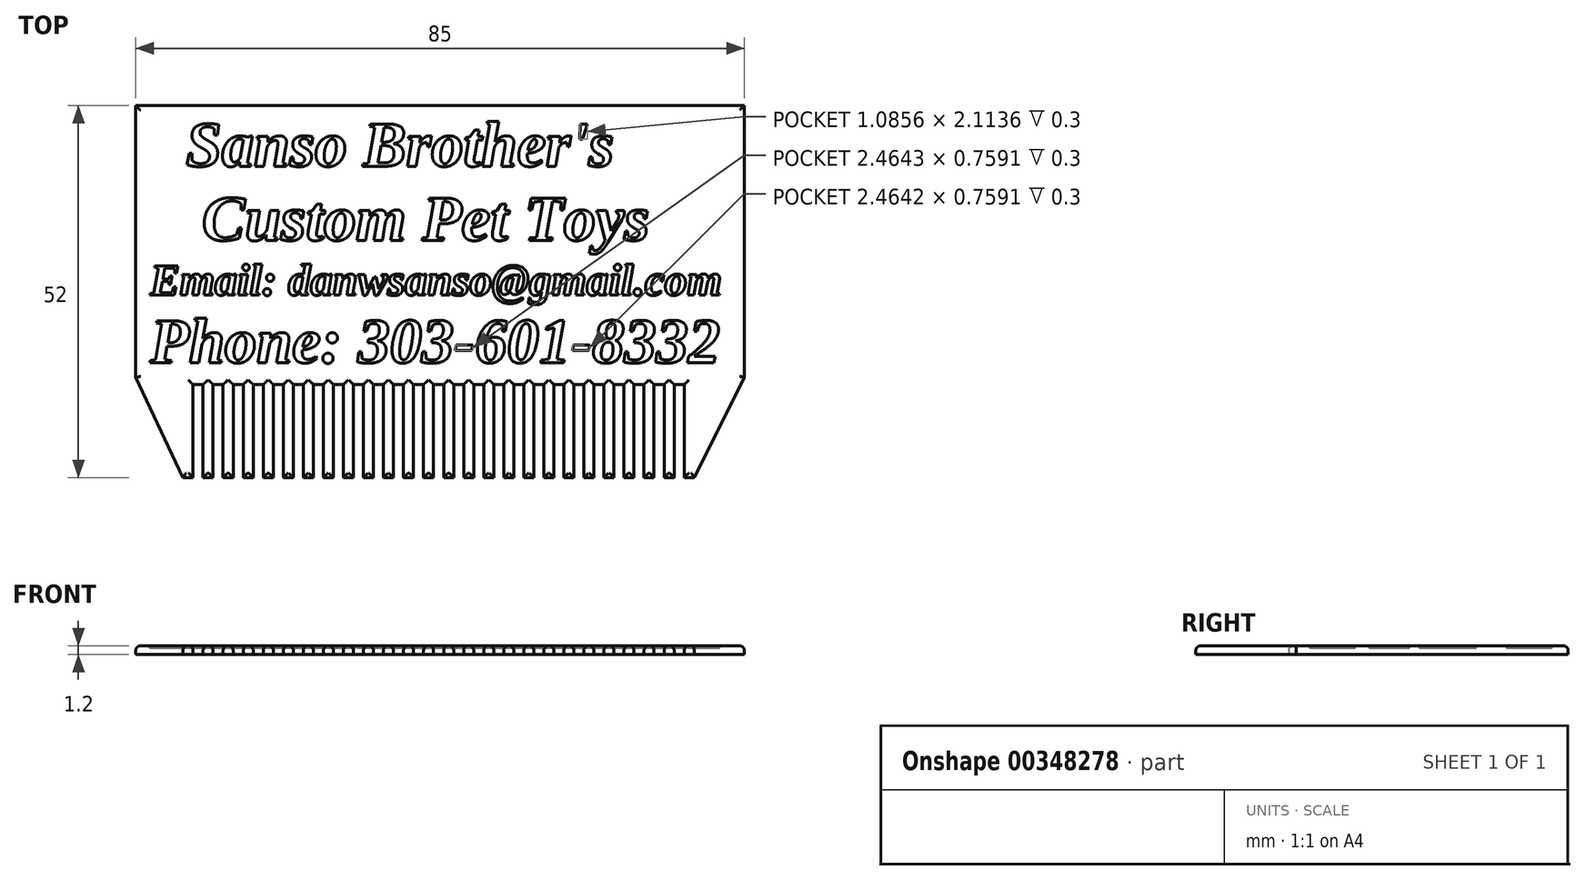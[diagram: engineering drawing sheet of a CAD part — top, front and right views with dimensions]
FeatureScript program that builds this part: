
annotation { "Feature Type Name" : "Feature", "Feature Type Description" : "" }
export const myFeature = defineFeature(function(context is Context, id is Id, definition is map)
    precondition{}
    {
        {
            var Q0;
            Q0=qCreatedBy(makeId("Top.planeOp"),FACE);
            var sketch = newSketch(context, id + "F0", { "sketchPlane" : qUnion([Q0])});
            skLineSegment(sketch, "E0.bottom", {"start": v(-26, -42.5) * mm, "end": v(-26, -80.5) * mm});
            skLineSegment(sketch, "E0.top", {"start": v(59, -42.5) * mm, "end": v(59, -80.5) * mm});
            skLineSegment(sketch, "E0.left", {"start": v(-26, -42.5) * mm, "end": v(59, -42.5) * mm});
            skLineSegment(sketch, "E0.right", {"start": v(-19.4, -94.5) * mm, "end": v(-18, -94.5) * mm});
            skPoint(sketch, "E0.middle", {"position": v(16.5, -68.5) * mm});
            skLineSegment(sketch, "E1", {"start": v(-18, -94.5) * mm, "end": v(-18, -81.5) * mm});
            skLineSegment(sketch, "E2", {"start": v(-18, -81.5) * mm, "end": v(-16.6, -81.5) * mm});
            skLineSegment(sketch, "E3", {"start": v(-16.6, -81.5) * mm, "end": v(-16.6, -94.5) * mm});
            skLineSegment(sketch, "E4.0.1.0", {"start": v(-16.6, -94.5) * mm, "end": v(-16.6, -81.5) * mm});
            skLineSegment(sketch, "E4.0.1.1", {"start": v(-15.2, -81.5) * mm, "end": v(-15.2, -94.5) * mm});
            skLineSegment(sketch, "E4.0.2.0", {"start": v(-15.2, -94.5) * mm, "end": v(-15.2, -81.5) * mm});
            skLineSegment(sketch, "E4.0.2.1", {"start": v(-13.8, -81.5) * mm, "end": v(-13.8, -94.5) * mm});
            skLineSegment(sketch, "E4.0.2.2", {"start": v(-15.2, -81.5) * mm, "end": v(-13.8, -81.5) * mm});
            skLineSegment(sketch, "E4.0.3.0", {"start": v(-13.8, -94.5) * mm, "end": v(-13.8, -81.5) * mm});
            skLineSegment(sketch, "E4.0.3.1", {"start": v(-12.4, -81.5) * mm, "end": v(-12.4, -94.5) * mm});
            skLineSegment(sketch, "E4.0.4.0", {"start": v(-12.4, -94.5) * mm, "end": v(-12.4, -81.5) * mm});
            skLineSegment(sketch, "E4.0.4.1", {"start": v(-11, -81.5) * mm, "end": v(-11, -94.5) * mm});
            skLineSegment(sketch, "E4.0.4.2", {"start": v(-12.4, -81.5) * mm, "end": v(-11, -81.5) * mm});
            skLineSegment(sketch, "E4.0.5.0", {"start": v(-11, -94.5) * mm, "end": v(-11, -81.5) * mm});
            skLineSegment(sketch, "E4.0.5.1", {"start": v(-9.6, -81.5) * mm, "end": v(-9.6, -94.5) * mm});
            skLineSegment(sketch, "E4.0.6.0", {"start": v(-9.6, -94.5) * mm, "end": v(-9.6, -81.5) * mm});
            skLineSegment(sketch, "E4.0.6.1", {"start": v(-8.2, -81.5) * mm, "end": v(-8.2, -94.5) * mm});
            skLineSegment(sketch, "E4.0.6.2", {"start": v(-9.6, -81.5) * mm, "end": v(-8.2, -81.5) * mm});
            skLineSegment(sketch, "E4.0.7.0", {"start": v(-8.2, -94.5) * mm, "end": v(-8.2, -81.5) * mm});
            skLineSegment(sketch, "E4.0.7.1", {"start": v(-6.8, -81.5) * mm, "end": v(-6.8, -94.5) * mm});
            skLineSegment(sketch, "E4.0.8.0", {"start": v(-6.8, -94.5) * mm, "end": v(-6.8, -81.5) * mm});
            skLineSegment(sketch, "E4.0.8.1", {"start": v(-5.4, -81.5) * mm, "end": v(-5.4, -94.5) * mm});
            skLineSegment(sketch, "E4.0.8.2", {"start": v(-6.8, -81.5) * mm, "end": v(-5.4, -81.5) * mm});
            skLineSegment(sketch, "E4.0.9.0", {"start": v(-5.4, -94.5) * mm, "end": v(-5.4, -81.5) * mm});
            skLineSegment(sketch, "E4.0.9.1", {"start": v(-4, -81.5) * mm, "end": v(-4, -94.5) * mm});
            skLineSegment(sketch, "E4.0.10.0", {"start": v(-4, -94.5) * mm, "end": v(-4, -81.5) * mm});
            skLineSegment(sketch, "E4.0.10.1", {"start": v(-2.6, -81.5) * mm, "end": v(-2.6, -94.5) * mm});
            skLineSegment(sketch, "E4.0.10.2", {"start": v(-4, -81.5) * mm, "end": v(-2.6, -81.5) * mm});
            skLineSegment(sketch, "E4.0.11.0", {"start": v(-2.6, -94.5) * mm, "end": v(-2.6, -81.5) * mm});
            skLineSegment(sketch, "E4.0.11.1", {"start": v(-1.2, -81.5) * mm, "end": v(-1.2, -94.5) * mm});
            skLineSegment(sketch, "E4.0.12.0", {"start": v(-1.2, -94.5) * mm, "end": v(-1.2, -81.5) * mm});
            skLineSegment(sketch, "E4.0.12.1", {"start": v(0.2, -81.5) * mm, "end": v(0.2, -94.5) * mm});
            skLineSegment(sketch, "E4.0.12.2", {"start": v(-1.2, -81.5) * mm, "end": v(0.2, -81.5) * mm});
            skLineSegment(sketch, "E4.0.13.0", {"start": v(0.2, -94.5) * mm, "end": v(0.2, -81.5) * mm});
            skLineSegment(sketch, "E4.0.13.1", {"start": v(1.6, -81.5) * mm, "end": v(1.6, -94.5) * mm});
            skLineSegment(sketch, "E4.0.14.0", {"start": v(1.6, -94.5) * mm, "end": v(1.6, -81.5) * mm});
            skLineSegment(sketch, "E4.0.14.1", {"start": v(3, -81.5) * mm, "end": v(3, -94.5) * mm});
            skLineSegment(sketch, "E4.0.14.2", {"start": v(1.6, -81.5) * mm, "end": v(3, -81.5) * mm});
            skLineSegment(sketch, "E4.0.15.0", {"start": v(3, -94.5) * mm, "end": v(3, -81.5) * mm});
            skLineSegment(sketch, "E4.0.15.1", {"start": v(4.4, -81.5) * mm, "end": v(4.4, -94.5) * mm});
            skLineSegment(sketch, "E4.0.16.0", {"start": v(4.4, -94.5) * mm, "end": v(4.4, -81.5) * mm});
            skLineSegment(sketch, "E4.0.16.1", {"start": v(5.8, -81.5) * mm, "end": v(5.8, -94.5) * mm});
            skLineSegment(sketch, "E4.0.16.2", {"start": v(4.4, -81.5) * mm, "end": v(5.8, -81.5) * mm});
            skLineSegment(sketch, "E4.0.17.0", {"start": v(5.8, -94.5) * mm, "end": v(5.8, -81.5) * mm});
            skLineSegment(sketch, "E4.0.17.1", {"start": v(7.2, -81.5) * mm, "end": v(7.2, -94.5) * mm});
            skLineSegment(sketch, "E4.0.18.0", {"start": v(7.2, -94.5) * mm, "end": v(7.2, -81.5) * mm});
            skLineSegment(sketch, "E4.0.18.1", {"start": v(8.6, -81.5) * mm, "end": v(8.6, -94.5) * mm});
            skLineSegment(sketch, "E4.0.18.2", {"start": v(7.2, -81.5) * mm, "end": v(8.6, -81.5) * mm});
            skLineSegment(sketch, "E4.0.19.0", {"start": v(8.6, -94.5) * mm, "end": v(8.6, -81.5) * mm});
            skLineSegment(sketch, "E4.0.19.1", {"start": v(10, -81.5) * mm, "end": v(10, -94.5) * mm});
            skLineSegment(sketch, "E4.0.20.0", {"start": v(10, -94.5) * mm, "end": v(10, -81.5) * mm});
            skLineSegment(sketch, "E4.0.20.1", {"start": v(11.4, -81.5) * mm, "end": v(11.4, -94.5) * mm});
            skLineSegment(sketch, "E4.0.20.2", {"start": v(10, -81.5) * mm, "end": v(11.4, -81.5) * mm});
            skLineSegment(sketch, "E4.0.21.0", {"start": v(11.4, -94.5) * mm, "end": v(11.4, -81.5) * mm});
            skLineSegment(sketch, "E4.0.21.1", {"start": v(12.8, -81.5) * mm, "end": v(12.8, -94.5) * mm});
            skLineSegment(sketch, "E4.0.22.0", {"start": v(12.8, -94.5) * mm, "end": v(12.8, -81.5) * mm});
            skLineSegment(sketch, "E4.0.22.1", {"start": v(14.2, -81.5) * mm, "end": v(14.2, -94.5) * mm});
            skLineSegment(sketch, "E4.0.22.2", {"start": v(12.8, -81.5) * mm, "end": v(14.2, -81.5) * mm});
            skLineSegment(sketch, "E4.0.23.0", {"start": v(14.2, -94.5) * mm, "end": v(14.2, -81.5) * mm});
            skLineSegment(sketch, "E4.0.23.1", {"start": v(15.6, -81.5) * mm, "end": v(15.6, -94.5) * mm});
            skLineSegment(sketch, "E4.0.24.0", {"start": v(15.6, -94.5) * mm, "end": v(15.6, -81.5) * mm});
            skLineSegment(sketch, "E4.0.24.1", {"start": v(17, -81.5) * mm, "end": v(17, -94.5) * mm});
            skLineSegment(sketch, "E4.0.24.2", {"start": v(15.6, -81.5) * mm, "end": v(17, -81.5) * mm});
            skLineSegment(sketch, "E4.0.25.0", {"start": v(17, -94.5) * mm, "end": v(17, -81.5) * mm});
            skLineSegment(sketch, "E4.0.25.1", {"start": v(18.4, -81.5) * mm, "end": v(18.4, -94.5) * mm});
            skLineSegment(sketch, "E4.0.26.0", {"start": v(18.4, -94.5) * mm, "end": v(18.4, -81.5) * mm});
            skLineSegment(sketch, "E4.0.26.1", {"start": v(19.8, -81.5) * mm, "end": v(19.8, -94.5) * mm});
            skLineSegment(sketch, "E4.0.26.2", {"start": v(18.4, -81.5) * mm, "end": v(19.8, -81.5) * mm});
            skLineSegment(sketch, "E4.0.27.0", {"start": v(19.8, -94.5) * mm, "end": v(19.8, -81.5) * mm});
            skLineSegment(sketch, "E4.0.27.1", {"start": v(21.2, -81.5) * mm, "end": v(21.2, -94.5) * mm});
            skLineSegment(sketch, "E4.0.28.0", {"start": v(21.2, -94.5) * mm, "end": v(21.2, -81.5) * mm});
            skLineSegment(sketch, "E4.0.28.1", {"start": v(22.6, -81.5) * mm, "end": v(22.6, -94.5) * mm});
            skLineSegment(sketch, "E4.0.28.2", {"start": v(21.2, -81.5) * mm, "end": v(22.6, -81.5) * mm});
            skLineSegment(sketch, "E4.0.29.0", {"start": v(22.6, -94.5) * mm, "end": v(22.6, -81.5) * mm});
            skLineSegment(sketch, "E4.0.29.1", {"start": v(24, -81.5) * mm, "end": v(24, -94.5) * mm});
            skLineSegment(sketch, "E4.0.30.0", {"start": v(24, -94.5) * mm, "end": v(24, -81.5) * mm});
            skLineSegment(sketch, "E4.0.30.1", {"start": v(25.4, -81.5) * mm, "end": v(25.4, -94.5) * mm});
            skLineSegment(sketch, "E4.0.30.2", {"start": v(24, -81.5) * mm, "end": v(25.4, -81.5) * mm});
            skLineSegment(sketch, "E4.0.31.0", {"start": v(25.4, -94.5) * mm, "end": v(25.4, -81.5) * mm});
            skLineSegment(sketch, "E4.0.31.1", {"start": v(26.8, -81.5) * mm, "end": v(26.8, -94.5) * mm});
            skLineSegment(sketch, "E4.0.32.0", {"start": v(26.8, -94.5) * mm, "end": v(26.8, -81.5) * mm});
            skLineSegment(sketch, "E4.0.32.1", {"start": v(28.2, -81.5) * mm, "end": v(28.2, -94.5) * mm});
            skLineSegment(sketch, "E4.0.32.2", {"start": v(26.8, -81.5) * mm, "end": v(28.2, -81.5) * mm});
            skLineSegment(sketch, "E4.0.33.0", {"start": v(28.2, -94.5) * mm, "end": v(28.2, -81.5) * mm});
            skLineSegment(sketch, "E4.0.33.1", {"start": v(29.6, -81.5) * mm, "end": v(29.6, -94.5) * mm});
            skLineSegment(sketch, "E4.0.34.0", {"start": v(29.6, -94.5) * mm, "end": v(29.6, -81.5) * mm});
            skLineSegment(sketch, "E4.0.34.1", {"start": v(31, -81.5) * mm, "end": v(31, -94.5) * mm});
            skLineSegment(sketch, "E4.0.34.2", {"start": v(29.6, -81.5) * mm, "end": v(31, -81.5) * mm});
            skLineSegment(sketch, "E4.0.35.0", {"start": v(31, -94.5) * mm, "end": v(31, -81.5) * mm});
            skLineSegment(sketch, "E4.0.35.1", {"start": v(32.4, -81.5) * mm, "end": v(32.4, -94.5) * mm});
            skLineSegment(sketch, "E4.0.36.0", {"start": v(32.4, -94.5) * mm, "end": v(32.4, -81.5) * mm});
            skLineSegment(sketch, "E4.0.36.1", {"start": v(33.8, -81.5) * mm, "end": v(33.8, -94.5) * mm});
            skLineSegment(sketch, "E4.0.36.2", {"start": v(32.4, -81.5) * mm, "end": v(33.8, -81.5) * mm});
            skLineSegment(sketch, "E4.0.37.0", {"start": v(33.8, -94.5) * mm, "end": v(33.8, -81.5) * mm});
            skLineSegment(sketch, "E4.0.37.1", {"start": v(35.2, -81.5) * mm, "end": v(35.2, -94.5) * mm});
            skLineSegment(sketch, "E4.0.38.0", {"start": v(35.2, -94.5) * mm, "end": v(35.2, -81.5) * mm});
            skLineSegment(sketch, "E4.0.38.1", {"start": v(36.6, -81.5) * mm, "end": v(36.6, -94.5) * mm});
            skLineSegment(sketch, "E4.0.38.2", {"start": v(35.2, -81.5) * mm, "end": v(36.6, -81.5) * mm});
            skLineSegment(sketch, "E4.0.39.0", {"start": v(36.6, -94.5) * mm, "end": v(36.6, -81.5) * mm});
            skLineSegment(sketch, "E4.0.39.1", {"start": v(38, -81.5) * mm, "end": v(38, -94.5) * mm});
            skLineSegment(sketch, "E4.0.40.0", {"start": v(38, -94.5) * mm, "end": v(38, -81.5) * mm});
            skLineSegment(sketch, "E4.0.40.1", {"start": v(39.4, -81.5) * mm, "end": v(39.4, -94.5) * mm});
            skLineSegment(sketch, "E4.0.40.2", {"start": v(38, -81.5) * mm, "end": v(39.4, -81.5) * mm});
            skLineSegment(sketch, "E4.0.41.0", {"start": v(39.4, -94.5) * mm, "end": v(39.4, -81.5) * mm});
            skLineSegment(sketch, "E4.0.41.1", {"start": v(40.8, -81.5) * mm, "end": v(40.8, -94.5) * mm});
            skLineSegment(sketch, "E4.0.42.0", {"start": v(40.8, -94.5) * mm, "end": v(40.8, -81.5) * mm});
            skLineSegment(sketch, "E4.0.42.1", {"start": v(42.2, -81.5) * mm, "end": v(42.2, -94.5) * mm});
            skLineSegment(sketch, "E4.0.42.2", {"start": v(40.8, -81.5) * mm, "end": v(42.2, -81.5) * mm});
            skLineSegment(sketch, "E4.0.43.0", {"start": v(42.2, -94.5) * mm, "end": v(42.2, -81.5) * mm});
            skLineSegment(sketch, "E4.0.43.1", {"start": v(43.6, -81.5) * mm, "end": v(43.6, -94.5) * mm});
            skLineSegment(sketch, "E4.0.44.0", {"start": v(43.6, -94.5) * mm, "end": v(43.6, -81.5) * mm});
            skLineSegment(sketch, "E4.0.44.1", {"start": v(45, -81.5) * mm, "end": v(45, -94.5) * mm});
            skLineSegment(sketch, "E4.0.44.2", {"start": v(43.6, -81.5) * mm, "end": v(45, -81.5) * mm});
            skLineSegment(sketch, "E4.0.45.0", {"start": v(45, -94.5) * mm, "end": v(45, -81.5) * mm});
            skLineSegment(sketch, "E4.0.45.1", {"start": v(46.4, -81.5) * mm, "end": v(46.4, -94.5) * mm});
            skLineSegment(sketch, "E4.0.46.0", {"start": v(46.4, -94.5) * mm, "end": v(46.4, -81.5) * mm});
            skLineSegment(sketch, "E4.0.46.1", {"start": v(47.8, -81.5) * mm, "end": v(47.8, -94.5) * mm});
            skLineSegment(sketch, "E4.0.46.2", {"start": v(46.4, -81.5) * mm, "end": v(47.8, -81.5) * mm});
            skLineSegment(sketch, "E4.0.47.0", {"start": v(47.8, -94.5) * mm, "end": v(47.8, -81.5) * mm});
            skLineSegment(sketch, "E4.0.47.1", {"start": v(49.2, -81.5) * mm, "end": v(49.2, -94.5) * mm});
            skLineSegment(sketch, "E4.0.48.0", {"start": v(49.2, -94.5) * mm, "end": v(49.2, -81.5) * mm});
            skLineSegment(sketch, "E4.0.48.1", {"start": v(50.6, -81.5) * mm, "end": v(50.6, -94.5) * mm});
            skLineSegment(sketch, "E4.0.48.2", {"start": v(49.2, -81.5) * mm, "end": v(50.6, -81.5) * mm});
            skLineSegment(sketch, "E4.0.49.0", {"start": v(50.6, -94.5) * mm, "end": v(50.6, -81.5) * mm});
            skLineSegment(sketch, "E4.direction1", {"start": v(-21.58, -80.5) * mm, "end": v(-21.58, -91.6) * mm, "construction": true});
            skLineSegment(sketch, "E4.direction2", {"start": v(-21.58, -80.5) * mm, "end": v(-17.6, -80.5) * mm, "construction": true});
            skLineSegment(sketch, "E5.trimOffspring", {"start": v(-16.6, -94.5) * mm, "end": v(-15.2, -94.5) * mm});
            skLineSegment(sketch, "E6.trimOffspring", {"start": v(-13.8, -94.5) * mm, "end": v(-12.4, -94.5) * mm});
            skLineSegment(sketch, "E7.trimOffspring", {"start": v(-11, -94.5) * mm, "end": v(-9.6, -94.5) * mm});
            skLineSegment(sketch, "E8.trimOffspring", {"start": v(-8.2, -94.5) * mm, "end": v(-6.8, -94.5) * mm});
            skLineSegment(sketch, "E9.trimOffspring", {"start": v(-5.4, -94.5) * mm, "end": v(-4, -94.5) * mm});
            skLineSegment(sketch, "E10.trimOffspring", {"start": v(-2.6, -94.5) * mm, "end": v(-1.2, -94.5) * mm});
            skLineSegment(sketch, "E11.trimOffspring", {"start": v(0.2, -94.5) * mm, "end": v(1.6, -94.5) * mm});
            skLineSegment(sketch, "E12.trimOffspring", {"start": v(3, -94.5) * mm, "end": v(4.4, -94.5) * mm});
            skLineSegment(sketch, "E13.trimOffspring", {"start": v(5.8, -94.5) * mm, "end": v(7.2, -94.5) * mm});
            skLineSegment(sketch, "E14.trimOffspring", {"start": v(8.6, -94.5) * mm, "end": v(10, -94.5) * mm});
            skLineSegment(sketch, "E15.trimOffspring", {"start": v(11.4, -94.5) * mm, "end": v(12.8, -94.5) * mm});
            skLineSegment(sketch, "E16.trimOffspring", {"start": v(14.2, -94.5) * mm, "end": v(15.6, -94.5) * mm});
            skLineSegment(sketch, "E17.trimOffspring", {"start": v(17, -94.5) * mm, "end": v(18.4, -94.5) * mm});
            skLineSegment(sketch, "E18.trimOffspring", {"start": v(19.8, -94.5) * mm, "end": v(21.2, -94.5) * mm});
            skLineSegment(sketch, "E19.trimOffspring", {"start": v(22.6, -94.5) * mm, "end": v(24, -94.5) * mm});
            skLineSegment(sketch, "E20.trimOffspring", {"start": v(25.4, -94.5) * mm, "end": v(26.8, -94.5) * mm});
            skLineSegment(sketch, "E21.trimOffspring", {"start": v(28.2, -94.5) * mm, "end": v(29.6, -94.5) * mm});
            skLineSegment(sketch, "E22.trimOffspring", {"start": v(31, -94.5) * mm, "end": v(32.4, -94.5) * mm});
            skLineSegment(sketch, "E23.trimOffspring", {"start": v(33.8, -94.5) * mm, "end": v(35.2, -94.5) * mm});
            skLineSegment(sketch, "E24.trimOffspring", {"start": v(36.6, -94.5) * mm, "end": v(38, -94.5) * mm});
            skLineSegment(sketch, "E25.trimOffspring", {"start": v(39.4, -94.5) * mm, "end": v(40.8, -94.5) * mm});
            skLineSegment(sketch, "E26.trimOffspring", {"start": v(42.2, -94.5) * mm, "end": v(43.6, -94.5) * mm});
            skLineSegment(sketch, "E27.trimOffspring", {"start": v(45, -94.5) * mm, "end": v(46.4, -94.5) * mm});
            skLineSegment(sketch, "E28.trimOffspring", {"start": v(47.8, -94.5) * mm, "end": v(49.2, -94.5) * mm});
            skLineSegment(sketch, "E29.trimOffspring", {"start": v(50.6, -94.5) * mm, "end": v(52, -94.5) * mm});
            skLineSegment(sketch, "E30", {"start": v(-19.4, -94.5) * mm, "end": v(-26, -80.5) * mm});
            skLineSegment(sketch, "E31", {"start": v(52, -94.5) * mm, "end": v(59, -80.5) * mm});
            skPoint(sketch, "E32.orphan", {"position": v(-26, -94.5) * mm});
            skPoint(sketch, "E33.orphan", {"position": v(59, -94.5) * mm});
            skSolve(sketch);
        }
        {
            var Q0;
            Q0 = qSketchRegion(id + "F0", true);
            extrude(context, id + "F1", {"entities" : qUnion([Q0]), "depth" : 1.2 * mm, "offsetDistance" : 25 * mm});
        }
        {
            var Q0;
            Q0=makeQuery(id+"F1.opExtrude","CAP_EDGE",EDGE,{"disambiguationData":[OSD([sQuery(id+"F0.wireOp",EDGE,"E5.trimOffspring")])],"isStart":false});
            var Q1;
            Q1=makeQuery(id+"F1.opExtrude","CAP_FACE",FACE,{"disambiguationData":[OSD([sQuery(id+"F0.wireOp",EDGE,"E0.bottom"),sQuery(id+"F0.wireOp",EDGE,"E0.top"),sQuery(id+"F0.wireOp",EDGE,"E0.left"),sQuery(id+"F0.wireOp",EDGE,"E0.right"),sQuery(id+"F0.wireOp",EDGE,"E1"),sQuery(id+"F0.wireOp",EDGE,"E2"),sQuery(id+"F0.wireOp",EDGE,"E4.0.1.0"),sQuery(id+"F0.wireOp",EDGE,"E4.0.2.0"),sQuery(id+"F0.wireOp",EDGE,"E4.0.2.2"),sQuery(id+"F0.wireOp",EDGE,"E4.0.3.0"),sQuery(id+"F0.wireOp",EDGE,"E4.0.4.0"),sQuery(id+"F0.wireOp",EDGE,"E4.0.4.2"),sQuery(id+"F0.wireOp",EDGE,"E4.0.5.0"),sQuery(id+"F0.wireOp",EDGE,"E4.0.6.0"),sQuery(id+"F0.wireOp",EDGE,"E4.0.6.2"),sQuery(id+"F0.wireOp",EDGE,"E4.0.7.0"),sQuery(id+"F0.wireOp",EDGE,"E4.0.8.0"),sQuery(id+"F0.wireOp",EDGE,"E4.0.8.2"),sQuery(id+"F0.wireOp",EDGE,"E4.0.9.0"),sQuery(id+"F0.wireOp",EDGE,"E4.0.10.0"),sQuery(id+"F0.wireOp",EDGE,"E4.0.10.2"),sQuery(id+"F0.wireOp",EDGE,"E4.0.11.0"),sQuery(id+"F0.wireOp",EDGE,"E4.0.12.0"),sQuery(id+"F0.wireOp",EDGE,"E4.0.12.2"),sQuery(id+"F0.wireOp",EDGE,"E4.0.13.0"),sQuery(id+"F0.wireOp",EDGE,"E4.0.14.0"),sQuery(id+"F0.wireOp",EDGE,"E4.0.14.2"),sQuery(id+"F0.wireOp",EDGE,"E4.0.15.0"),sQuery(id+"F0.wireOp",EDGE,"E4.0.16.0"),sQuery(id+"F0.wireOp",EDGE,"E4.0.16.2"),sQuery(id+"F0.wireOp",EDGE,"E4.0.17.0"),sQuery(id+"F0.wireOp",EDGE,"E4.0.18.0"),sQuery(id+"F0.wireOp",EDGE,"E4.0.18.2"),sQuery(id+"F0.wireOp",EDGE,"E4.0.19.0"),sQuery(id+"F0.wireOp",EDGE,"E4.0.20.0"),sQuery(id+"F0.wireOp",EDGE,"E4.0.20.2"),sQuery(id+"F0.wireOp",EDGE,"E4.0.21.0"),sQuery(id+"F0.wireOp",EDGE,"E4.0.22.0"),sQuery(id+"F0.wireOp",EDGE,"E4.0.22.2"),sQuery(id+"F0.wireOp",EDGE,"E4.0.23.0"),sQuery(id+"F0.wireOp",EDGE,"E4.0.24.0"),sQuery(id+"F0.wireOp",EDGE,"E4.0.24.2"),sQuery(id+"F0.wireOp",EDGE,"E4.0.25.0"),sQuery(id+"F0.wireOp",EDGE,"E4.0.26.0"),sQuery(id+"F0.wireOp",EDGE,"E4.0.26.2"),sQuery(id+"F0.wireOp",EDGE,"E4.0.27.0"),sQuery(id+"F0.wireOp",EDGE,"E4.0.28.0"),sQuery(id+"F0.wireOp",EDGE,"E4.0.28.2"),sQuery(id+"F0.wireOp",EDGE,"E4.0.29.0"),sQuery(id+"F0.wireOp",EDGE,"E4.0.30.0"),sQuery(id+"F0.wireOp",EDGE,"E4.0.30.2"),sQuery(id+"F0.wireOp",EDGE,"E4.0.31.0"),sQuery(id+"F0.wireOp",EDGE,"E4.0.32.0"),sQuery(id+"F0.wireOp",EDGE,"E4.0.32.2"),sQuery(id+"F0.wireOp",EDGE,"E4.0.33.0"),sQuery(id+"F0.wireOp",EDGE,"E4.0.34.0"),sQuery(id+"F0.wireOp",EDGE,"E4.0.34.2"),sQuery(id+"F0.wireOp",EDGE,"E4.0.35.0"),sQuery(id+"F0.wireOp",EDGE,"E4.0.36.0"),sQuery(id+"F0.wireOp",EDGE,"E4.0.36.2"),sQuery(id+"F0.wireOp",EDGE,"E4.0.37.0"),sQuery(id+"F0.wireOp",EDGE,"E4.0.38.0"),sQuery(id+"F0.wireOp",EDGE,"E4.0.38.2"),sQuery(id+"F0.wireOp",EDGE,"E4.0.39.0"),sQuery(id+"F0.wireOp",EDGE,"E4.0.40.0"),sQuery(id+"F0.wireOp",EDGE,"E4.0.40.2"),sQuery(id+"F0.wireOp",EDGE,"E4.0.41.0"),sQuery(id+"F0.wireOp",EDGE,"E4.0.42.0"),sQuery(id+"F0.wireOp",EDGE,"E4.0.42.2"),sQuery(id+"F0.wireOp",EDGE,"E4.0.43.0"),sQuery(id+"F0.wireOp",EDGE,"E4.0.44.0"),sQuery(id+"F0.wireOp",EDGE,"E4.0.44.2"),sQuery(id+"F0.wireOp",EDGE,"E4.0.45.0"),sQuery(id+"F0.wireOp",EDGE,"E4.0.46.0"),sQuery(id+"F0.wireOp",EDGE,"E4.0.46.2"),sQuery(id+"F0.wireOp",EDGE,"E4.0.47.0"),sQuery(id+"F0.wireOp",EDGE,"E4.0.48.0"),sQuery(id+"F0.wireOp",EDGE,"E4.0.48.2"),sQuery(id+"F0.wireOp",EDGE,"E4.0.49.0"),sQuery(id+"F0.wireOp",EDGE,"E5.trimOffspring"),sQuery(id+"F0.wireOp",EDGE,"E6.trimOffspring"),sQuery(id+"F0.wireOp",EDGE,"E7.trimOffspring"),sQuery(id+"F0.wireOp",EDGE,"E8.trimOffspring"),sQuery(id+"F0.wireOp",EDGE,"E9.trimOffspring"),sQuery(id+"F0.wireOp",EDGE,"E10.trimOffspring"),sQuery(id+"F0.wireOp",EDGE,"E11.trimOffspring"),sQuery(id+"F0.wireOp",EDGE,"E12.trimOffspring"),sQuery(id+"F0.wireOp",EDGE,"E13.trimOffspring"),sQuery(id+"F0.wireOp",EDGE,"E14.trimOffspring"),sQuery(id+"F0.wireOp",EDGE,"E15.trimOffspring"),sQuery(id+"F0.wireOp",EDGE,"E16.trimOffspring"),sQuery(id+"F0.wireOp",EDGE,"E17.trimOffspring"),sQuery(id+"F0.wireOp",EDGE,"E18.trimOffspring"),sQuery(id+"F0.wireOp",EDGE,"E19.trimOffspring"),sQuery(id+"F0.wireOp",EDGE,"E20.trimOffspring"),sQuery(id+"F0.wireOp",EDGE,"E21.trimOffspring"),sQuery(id+"F0.wireOp",EDGE,"E22.trimOffspring"),sQuery(id+"F0.wireOp",EDGE,"E23.trimOffspring"),sQuery(id+"F0.wireOp",EDGE,"E24.trimOffspring"),sQuery(id+"F0.wireOp",EDGE,"E25.trimOffspring"),sQuery(id+"F0.wireOp",EDGE,"E26.trimOffspring"),sQuery(id+"F0.wireOp",EDGE,"E27.trimOffspring"),sQuery(id+"F0.wireOp",EDGE,"E28.trimOffspring"),sQuery(id+"F0.wireOp",EDGE,"E29.trimOffspring"),sQuery(id+"F0.wireOp",EDGE,"E30"),sQuery(id+"F0.wireOp",EDGE,"E31")])],"isStart":false});
            fillet(context, id + "F2", {"entities" : qUnion([Q0, Q1]), "radius" : .65 * mm, "tangentPropagation" : true, "allowEdgeOverflow" : false});
        }
        {
            var Q0;
            Q0=makeQuery(id+"F1.opExtrude","CAP_FACE",FACE,{"disambiguationData":[OSD([sQuery(id+"F0.wireOp",EDGE,"E0.bottom"),sQuery(id+"F0.wireOp",EDGE,"E0.top"),sQuery(id+"F0.wireOp",EDGE,"E0.left"),sQuery(id+"F0.wireOp",EDGE,"E0.right"),sQuery(id+"F0.wireOp",EDGE,"E1"),sQuery(id+"F0.wireOp",EDGE,"E2"),sQuery(id+"F0.wireOp",EDGE,"E4.0.1.0"),sQuery(id+"F0.wireOp",EDGE,"E4.0.2.0"),sQuery(id+"F0.wireOp",EDGE,"E4.0.2.2"),sQuery(id+"F0.wireOp",EDGE,"E4.0.3.0"),sQuery(id+"F0.wireOp",EDGE,"E4.0.4.0"),sQuery(id+"F0.wireOp",EDGE,"E4.0.4.2"),sQuery(id+"F0.wireOp",EDGE,"E4.0.5.0"),sQuery(id+"F0.wireOp",EDGE,"E4.0.6.0"),sQuery(id+"F0.wireOp",EDGE,"E4.0.6.2"),sQuery(id+"F0.wireOp",EDGE,"E4.0.7.0"),sQuery(id+"F0.wireOp",EDGE,"E4.0.8.0"),sQuery(id+"F0.wireOp",EDGE,"E4.0.8.2"),sQuery(id+"F0.wireOp",EDGE,"E4.0.9.0"),sQuery(id+"F0.wireOp",EDGE,"E4.0.10.0"),sQuery(id+"F0.wireOp",EDGE,"E4.0.10.2"),sQuery(id+"F0.wireOp",EDGE,"E4.0.11.0"),sQuery(id+"F0.wireOp",EDGE,"E4.0.12.0"),sQuery(id+"F0.wireOp",EDGE,"E4.0.12.2"),sQuery(id+"F0.wireOp",EDGE,"E4.0.13.0"),sQuery(id+"F0.wireOp",EDGE,"E4.0.14.0"),sQuery(id+"F0.wireOp",EDGE,"E4.0.14.2"),sQuery(id+"F0.wireOp",EDGE,"E4.0.15.0"),sQuery(id+"F0.wireOp",EDGE,"E4.0.16.0"),sQuery(id+"F0.wireOp",EDGE,"E4.0.16.2"),sQuery(id+"F0.wireOp",EDGE,"E4.0.17.0"),sQuery(id+"F0.wireOp",EDGE,"E4.0.18.0"),sQuery(id+"F0.wireOp",EDGE,"E4.0.18.2"),sQuery(id+"F0.wireOp",EDGE,"E4.0.19.0"),sQuery(id+"F0.wireOp",EDGE,"E4.0.20.0"),sQuery(id+"F0.wireOp",EDGE,"E4.0.20.2"),sQuery(id+"F0.wireOp",EDGE,"E4.0.21.0"),sQuery(id+"F0.wireOp",EDGE,"E4.0.22.0"),sQuery(id+"F0.wireOp",EDGE,"E4.0.22.2"),sQuery(id+"F0.wireOp",EDGE,"E4.0.23.0"),sQuery(id+"F0.wireOp",EDGE,"E4.0.24.0"),sQuery(id+"F0.wireOp",EDGE,"E4.0.24.2"),sQuery(id+"F0.wireOp",EDGE,"E4.0.25.0"),sQuery(id+"F0.wireOp",EDGE,"E4.0.26.0"),sQuery(id+"F0.wireOp",EDGE,"E4.0.26.2"),sQuery(id+"F0.wireOp",EDGE,"E4.0.27.0"),sQuery(id+"F0.wireOp",EDGE,"E4.0.28.0"),sQuery(id+"F0.wireOp",EDGE,"E4.0.28.2"),sQuery(id+"F0.wireOp",EDGE,"E4.0.29.0"),sQuery(id+"F0.wireOp",EDGE,"E4.0.30.0"),sQuery(id+"F0.wireOp",EDGE,"E4.0.30.2"),sQuery(id+"F0.wireOp",EDGE,"E4.0.31.0"),sQuery(id+"F0.wireOp",EDGE,"E4.0.32.0"),sQuery(id+"F0.wireOp",EDGE,"E4.0.32.2"),sQuery(id+"F0.wireOp",EDGE,"E4.0.33.0"),sQuery(id+"F0.wireOp",EDGE,"E4.0.34.0"),sQuery(id+"F0.wireOp",EDGE,"E4.0.34.2"),sQuery(id+"F0.wireOp",EDGE,"E4.0.35.0"),sQuery(id+"F0.wireOp",EDGE,"E4.0.36.0"),sQuery(id+"F0.wireOp",EDGE,"E4.0.36.2"),sQuery(id+"F0.wireOp",EDGE,"E4.0.37.0"),sQuery(id+"F0.wireOp",EDGE,"E4.0.38.0"),sQuery(id+"F0.wireOp",EDGE,"E4.0.38.2"),sQuery(id+"F0.wireOp",EDGE,"E4.0.39.0"),sQuery(id+"F0.wireOp",EDGE,"E4.0.40.0"),sQuery(id+"F0.wireOp",EDGE,"E4.0.40.2"),sQuery(id+"F0.wireOp",EDGE,"E4.0.41.0"),sQuery(id+"F0.wireOp",EDGE,"E4.0.42.0"),sQuery(id+"F0.wireOp",EDGE,"E4.0.42.2"),sQuery(id+"F0.wireOp",EDGE,"E4.0.43.0"),sQuery(id+"F0.wireOp",EDGE,"E4.0.44.0"),sQuery(id+"F0.wireOp",EDGE,"E4.0.44.2"),sQuery(id+"F0.wireOp",EDGE,"E4.0.45.0"),sQuery(id+"F0.wireOp",EDGE,"E4.0.46.0"),sQuery(id+"F0.wireOp",EDGE,"E4.0.46.2"),sQuery(id+"F0.wireOp",EDGE,"E4.0.47.0"),sQuery(id+"F0.wireOp",EDGE,"E4.0.48.0"),sQuery(id+"F0.wireOp",EDGE,"E4.0.48.2"),sQuery(id+"F0.wireOp",EDGE,"E4.0.49.0"),sQuery(id+"F0.wireOp",EDGE,"E5.trimOffspring"),sQuery(id+"F0.wireOp",EDGE,"E6.trimOffspring"),sQuery(id+"F0.wireOp",EDGE,"E7.trimOffspring"),sQuery(id+"F0.wireOp",EDGE,"E8.trimOffspring"),sQuery(id+"F0.wireOp",EDGE,"E9.trimOffspring"),sQuery(id+"F0.wireOp",EDGE,"E10.trimOffspring"),sQuery(id+"F0.wireOp",EDGE,"E11.trimOffspring"),sQuery(id+"F0.wireOp",EDGE,"E12.trimOffspring"),sQuery(id+"F0.wireOp",EDGE,"E13.trimOffspring"),sQuery(id+"F0.wireOp",EDGE,"E14.trimOffspring"),sQuery(id+"F0.wireOp",EDGE,"E15.trimOffspring"),sQuery(id+"F0.wireOp",EDGE,"E16.trimOffspring"),sQuery(id+"F0.wireOp",EDGE,"E17.trimOffspring"),sQuery(id+"F0.wireOp",EDGE,"E18.trimOffspring"),sQuery(id+"F0.wireOp",EDGE,"E19.trimOffspring"),sQuery(id+"F0.wireOp",EDGE,"E20.trimOffspring"),sQuery(id+"F0.wireOp",EDGE,"E21.trimOffspring"),sQuery(id+"F0.wireOp",EDGE,"E22.trimOffspring"),sQuery(id+"F0.wireOp",EDGE,"E23.trimOffspring"),sQuery(id+"F0.wireOp",EDGE,"E24.trimOffspring"),sQuery(id+"F0.wireOp",EDGE,"E25.trimOffspring"),sQuery(id+"F0.wireOp",EDGE,"E26.trimOffspring"),sQuery(id+"F0.wireOp",EDGE,"E27.trimOffspring"),sQuery(id+"F0.wireOp",EDGE,"E28.trimOffspring"),sQuery(id+"F0.wireOp",EDGE,"E29.trimOffspring"),sQuery(id+"F0.wireOp",EDGE,"E30"),sQuery(id+"F0.wireOp",EDGE,"E31")])],"isStart":false});
            var sketch = newSketch(context, id + "F3", { "sketchPlane" : qUnion([Q0])});
            skText(sketch, "E34", { "text": "Sanso Brother\'s\n Custom Pet Toys", "fontName": "Tinos-BoldItalic.ttf"});
            skText(sketch, "E35", { "text": "Email: <email>", "fontName": "Tinos-BoldItalic.ttf"});
            skText(sketch, "E36", { "text": "Phone: 303-601-8332", "fontName": "Tinos-BoldItalic.ttf"});
            const initialGuessF3  = {"E34": [-0.019, -0.05098, 1, 0, 0.00648], "E35": [-0.024, -0.069, 1, 0, 0.0045], "E36": [-0.024, -0.07843, 1, 0, 0.00643]};
            skSetInitialGuess(sketch, initialGuessF3);
            skSolve(sketch);
        }
        {
            var Q0;
            Q0 = qSketchRegion(id + "F3", true);
            extrude(context, id + "F4", {"entities" : qUnion([Q0]), "operationType" : NewBodyOperationType.REMOVE, "oppositeDirection" : true, "depth" : .3 * mm, "offsetDistance" : 25 * mm});
        }
    });
